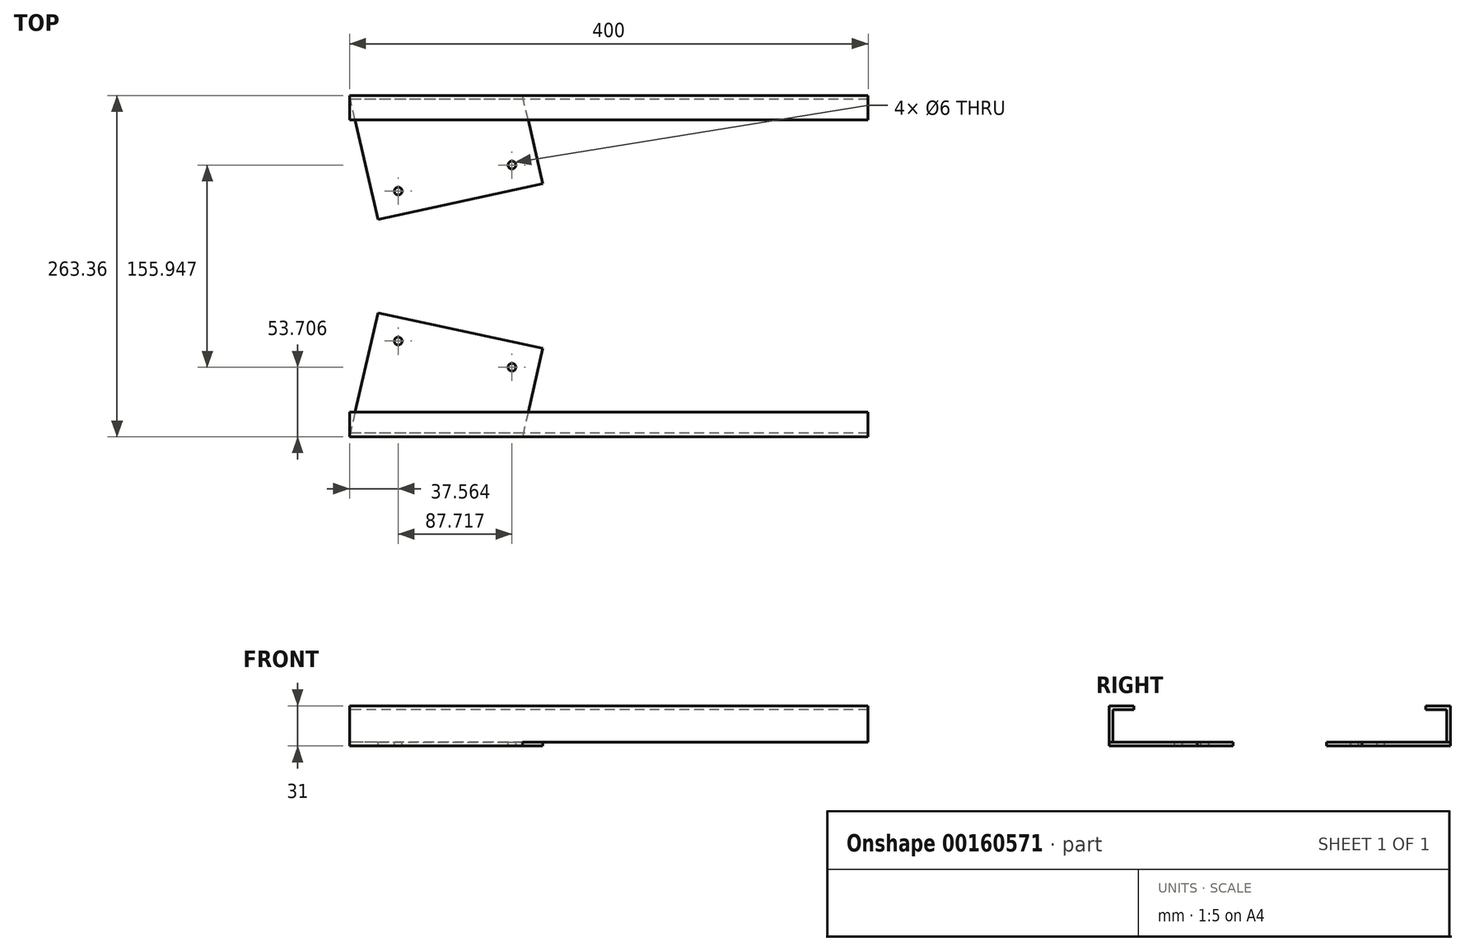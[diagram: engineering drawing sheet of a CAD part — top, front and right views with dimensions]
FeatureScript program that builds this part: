
annotation { "Feature Type Name" : "Feature", "Feature Type Description" : "" }
export const myFeature = defineFeature(function(context is Context, id is Id, definition is map)
    precondition{}
    {
        {
            var Q0;
            Q0=qCreatedBy(makeId("Top.planeOp"),FACE);
            var sketch = newSketch(context, id + "F0", { "sketchPlane" : qUnion([Q0])});
            skLineSegment(sketch, "E0.bottom", {"start": v(-218.62, 31.68) * mm, "end": v(181.38, 31.68) * mm});
            skLineSegment(sketch, "E0.top", {"start": v(-218.62, 12.68) * mm, "end": v(181.38, 12.68) * mm});
            skLineSegment(sketch, "E0.left", {"start": v(-218.62, 31.68) * mm, "end": v(-218.62, 12.68) * mm});
            skLineSegment(sketch, "E0.right", {"start": v(181.38, 31.68) * mm, "end": v(181.38, 12.68) * mm});
            skLineSegment(sketch, "E1", {"start": v(-218.62, 12.68) * mm, "end": v(-218.62, 15.68) * mm});
            skLineSegment(sketch, "E2", {"start": v(-218.62, 15.68) * mm, "end": v(181.38, 15.68) * mm});
            skLineSegment(sketch, "E3", {"start": v(-18.62, 31.68) * mm, "end": v(-18.62, 60.98) * mm});
            skSolve(sketch);
        }
        {
            var Q0;
            Q0=makeQuery(id+"F0.imprint","IMPRINT",FACE,{"disambiguationData":[TD([[makeQuery(id+"F0.imprint","IMPRINT",EDGE,{"derivedFrom":sQuery(id+"F0.wireOp",EDGE,"E0.bottom")}),-1.0]])]});
            var Q1;
            {var subQ0=sQuery(id+"F0.wireOp",EDGE,"E0.top");Q1=makeQuery(id+"F0.imprint","IMPRINT",FACE,{"disambiguationData":[TD([[makeQuery(id+"F0.imprint","IMPRINT",EDGE,{"derivedFrom":subQ0}),1.0]])]});}
            extrude(context, id + "F1", {"entities" : qUnion([Q0, Q1]), "depth" : 3 * mm});
        }
        {
            var Q0;
            Q0=qCreatedBy(makeId("Front.planeOp"),FACE);
            cPlane(context, id + "F2", {"entities" : qUnion([Q0]), "cplaneType" : CPlaneType.OFFSET, "offset" : 100 * mm, "width" : 150 * mm, "height" : 150 * mm});
        }
        {
            var Q0;
            {var subQ0=sQuery(id+"F0.wireOp",EDGE,"E0.top");Q0=makeQuery(id+"F0.imprint","IMPRINT",FACE,{"disambiguationData":[TD([[makeQuery(id+"F0.imprint","IMPRINT",EDGE,{"derivedFrom":subQ0}),1.0]])]});}
            extrude(context, id + "F3", {"entities" : qUnion([Q0]), "operationType" : NewBodyOperationType.ADD, "oppositeDirection" : true, "depth" : 25 * mm});
        }
        {
            var Q0;
            Q0=makeQuery(id+"F1.opExtrude","CAP_FACE",FACE,{"disambiguationData":[OSD([sQuery(id+"F0.wireOp",EDGE,"E0.bottom"),sQuery(id+"F0.wireOp",EDGE,"E0.top"),sQuery(id+"F0.wireOp",EDGE,"E0.left"),sQuery(id+"F0.wireOp",EDGE,"E0.right"),sQuery(id+"F0.wireOp",EDGE,"E1")])],"isStart":false});
            var sketch = newSketch(context, id + "F4", { "sketchPlane" : qUnion([Q0])});
            skLineSegment(sketch, "E4", {"start": v(181.38, 31.68) * mm, "end": v(181.38, 28.68) * mm});
            skLineSegment(sketch, "E5", {"start": v(181.38, 28.68) * mm, "end": v(-218.62, 28.68) * mm});
            skSolve(sketch);
        }
        {
            var Q0;
            Q0=makeQuery(id+"F4.imprint","IMPRINT",FACE,{"disambiguationData":[TD([[makeQuery(id+"F4.imprint","IMPRINT",EDGE,{"derivedFrom":sQuery(id+"F4.wireOp",EDGE,"E4")}),-1.0]])]});
            extrude(context, id + "F5", {"entities" : qUnion([Q0]), "operationType" : NewBodyOperationType.ADD, "oppositeDirection" : true, "depth" : 28 * mm});
        }
        {
            var Q0;
            Q0=makeQuery(id+"F5.opExtrude","CAP_FACE",FACE,{"disambiguationData":[OSD([sQuery(id+"F0.wireOp",EDGE,"E0.bottom"),sQuery(id+"F0.wireOp",EDGE,"E0.left"),sQuery(id+"F0.wireOp",EDGE,"E1"),sQuery(id+"F4.wireOp",EDGE,"E4"),sQuery(id+"F4.wireOp",EDGE,"E5")])],"isStart":false});
            var sketch = newSketch(context, id + "F6", { "sketchPlane" : qUnion([Q0])});
            skLineSegment(sketch, "E6", {"start": v(-196.54, 63.96) * mm, "end": v(-69.47, 36.53) * mm});
            skCircle(sketch, "E7", {"center": v(-181.06, 42.17) * mm, "radius": 3 * mm});
            skCircle(sketch, "E8", {"center": v(-93.34, 22.03) * mm, "radius": 3 * mm});
            skLineSegment(sketch, "E9", {"start": v(-196.54, 63.96) * mm, "end": v(-218.62, -31.68) * mm});
            skLineSegment(sketch, "E10", {"start": v(-93.34, 22.03) * mm, "end": v(-181.06, 42.17) * mm, "construction": true});
            skLineSegment(sketch, "E11", {"start": v(-181.06, 42.17) * mm, "end": v(-200.6, 46.4) * mm, "construction": true});
            skLineSegment(sketch, "E12", {"start": v(-69.47, 36.53) * mm, "end": v(-85.22, -31.68) * mm});
            skLineSegment(sketch, "E13", {"start": v(-93.34, 22.03) * mm, "end": v(-73.85, 17.55) * mm, "construction": true});
            skLineSegment(sketch, "E14", {"start": v(-84.53, -28.68) * mm, "end": v(-217.93, -28.68) * mm});
            skLineSegment(sketch, "E15", {"start": v(-214.24, -12.68) * mm, "end": v(-196.54, 63.96) * mm});
            skLineSegment(sketch, "E16", {"start": v(-80.9, -13.01) * mm, "end": v(-69.47, 36.53) * mm});
            skSolve(sketch);
        }
        {
            var Q0;
            {var subQ3=sQuery(id+"F6.wireOp",EDGE,"E14");Q0=makeQuery(id+"F6.imprint","IMPRINT",FACE,{"disambiguationData":[TD([[makeQuery(id+"F6.imprint","IMPRINT",EDGE,{"derivedFrom":subQ3}),1.0]])]});}
            var Q1;
            {var subQ1=sQuery(id+"F6.wireOp",EDGE,"E6");Q1=makeQuery(id+"F6.imprint","IMPRINT",FACE,{"disambiguationData":[TD([[makeQuery(id+"F6.imprint","IMPRINT",EDGE,{"derivedFrom":subQ1}),-1.0]])]});}
            extrude(context, id + "F7", {"entities" : qUnion([Q0, Q1]), "operationType" : NewBodyOperationType.ADD, "depth" : 3 * mm});
        }
        {
            var Q0;
            {var subQ0=sQuery(id+"F0.wireOp",EDGE,"E0.right");Q0=makeQuery(id+"F5.boolean.opBoolean","MERGE",FACE,{"derivedFrom":[makeQuery(id+"F3.boolean.opBoolean","MERGE",FACE,{"derivedFrom":[makeQuery(id+"F1.opExtrude","SWEPT_FACE",FACE,{"disambiguationData":[OSD([subQ0])]}),makeQuery(id+"F3.opExtrude","SWEPT_FACE",FACE,{"disambiguationData":[OSD([subQ0])]})]}),makeQuery(id+"F5.opExtrude","SWEPT_FACE",FACE,{"disambiguationData":[OSD([sQuery(id+"F4.wireOp",EDGE,"E4")])]})]});}
            var sketch = newSketch(context, id + "F8", { "sketchPlane" : qUnion([Q0])});
            skLineSegment(sketch, "E17", {"start": v(15.68, 0) * mm, "end": v(12.68, 0) * mm});
            skSolve(sketch);
        }
        {
            var Q0;
            {var subQ0=sQuery(id+"F8.wireOp",EDGE,"E17");Q0=makeQuery(id+"F8.imprint","IMPRINT",FACE,{"disambiguationData":[TD([[makeQuery(id+"F8.imprint","IMPRINT",EDGE,{"derivedFrom":subQ0}),1.0]])]});}
            extrude(context, id + "F9", {"entities" : qUnion([Q0]), "operationType" : NewBodyOperationType.REMOVE, "endBound" : BoundingType.THROUGH_ALL, "oppositeDirection" : true, "depth" : 25 * mm});
        }
        {
            var Q0;
            Q0=makeQuery(id+"F1.opExtrude","SWEPT_BODY",BODY,{"disambiguationData":[OSD([sQuery(id+"F0.wireOp",EDGE,"E0.bottom"),sQuery(id+"F0.wireOp",EDGE,"E0.top"),sQuery(id+"F0.wireOp",EDGE,"E0.left"),sQuery(id+"F0.wireOp",EDGE,"E0.right")])]});
            var Q1;
            Q1=makeQuery(id+"Ft6an8YSvDRpxkC_8.opExtrude","SWEPT_BODY",BODY,{"disambiguationData":[OSD([sQuery(id+"F0.wireOp",EDGE,"E0.bottom"),sQuery(id+"F0.wireOp",EDGE,"E0.top"),sQuery(id+"FvsTlPq3GS24Few_8.wireOp",EDGE,"2jAUF4hz-O2uM-nnLi-Vq91-Vjk8H5khP2AE"),sQuery(id+"FJNviUOJyLBGGWq_8.wireOp",EDGE,"JMyEuUKv-YXIB-msAy-wZmV-038ssuPIx9rc")])]});
            var Q2;
            Q2=qCreatedBy(id+"F2.planeOp",FACE);
            mirror(context, id + "F10", {"entities" : qUnion([Q0, Q1]), "mirrorPlane" : qUnion([Q2])});
        }
    });
